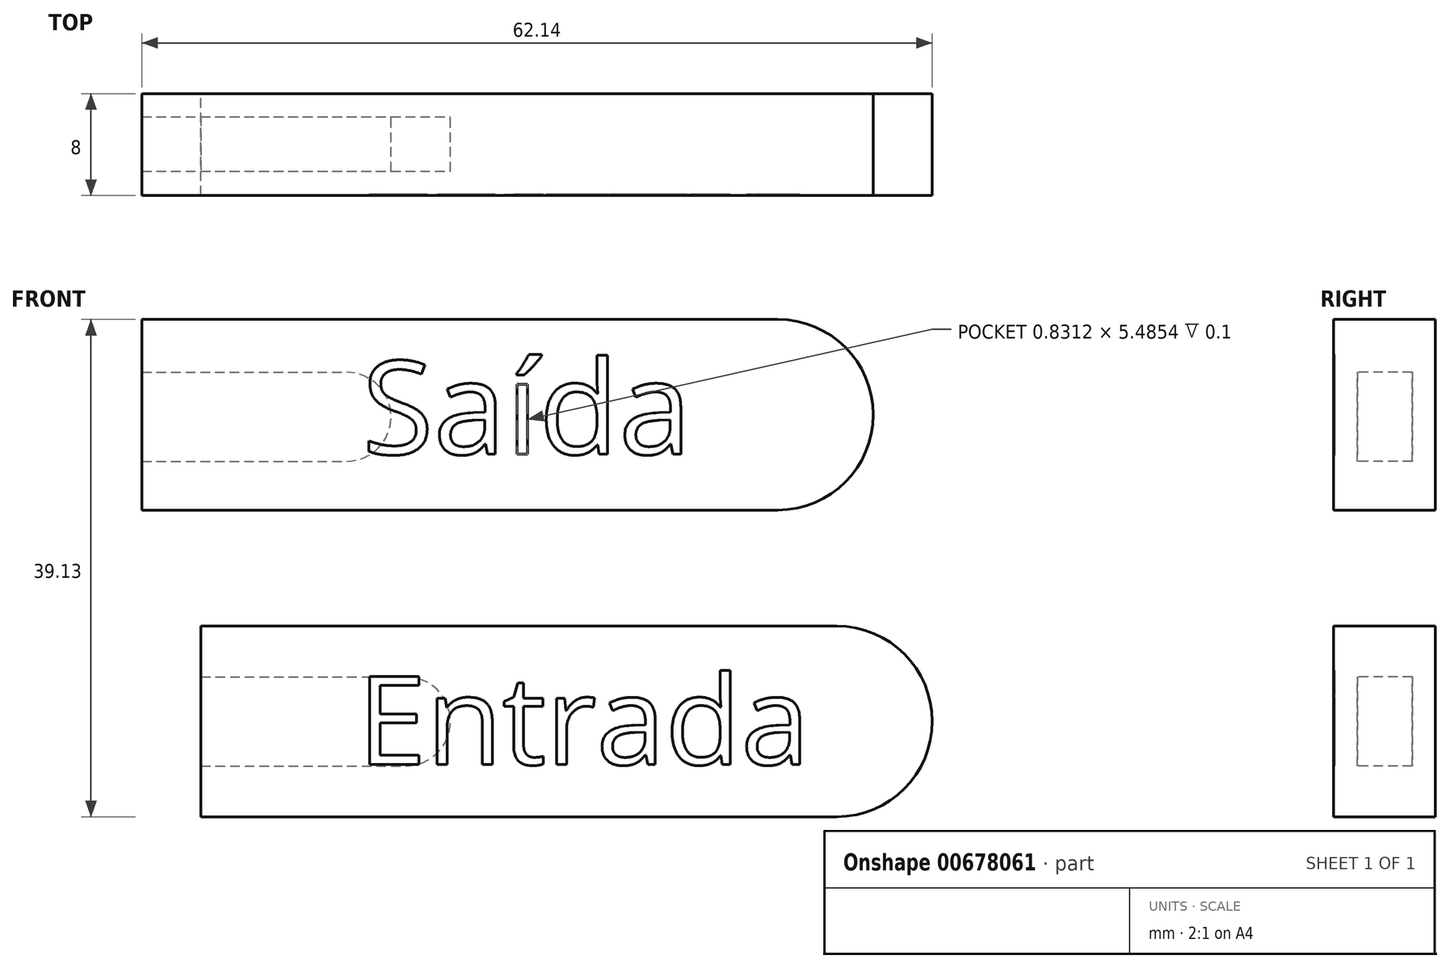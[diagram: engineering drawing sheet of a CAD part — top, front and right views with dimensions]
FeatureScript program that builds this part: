
annotation { "Feature Type Name" : "Feature", "Feature Type Description" : "" }
export const myFeature = defineFeature(function(context is Context, id is Id, definition is map)
    precondition{}
    {
        {
            var Q0;
            Q0=qCreatedBy(makeId("Front.planeOp"),FACE);
            var sketch = newSketch(context, id + "F0", { "sketchPlane" : qUnion([Q0])});
            skLineSegment(sketch, "E0", {"start": v(-53.67, -9.13) * mm, "end": v(-53.67, -24.13) * mm});
            skLineSegment(sketch, "E1", {"start": v(-53.67, -9.13) * mm, "end": v(-3.67, -9.13) * mm});
            skLineSegment(sketch, "E2", {"start": v(-53.67, -24.13) * mm, "end": v(-3.67, -24.13) * mm});
            skArc(sketch, "E3", {"start": v(-3.67, -24.13) * mm, "mid": v(3.83, -16.63) * mm, "end": v(-3.67, -9.13) * mm});
            skSolve(sketch);
        }
        {
            var Q0;
            Q0=makeQuery(id+"F0.imprint","IMPRINT",FACE,{"disambiguationData":[TD([[makeQuery(id+"F0.imprint","IMPRINT",EDGE,{"derivedFrom":sQuery(id+"F0.wireOp",EDGE,"E0")}),1.0]])]});
            extrude(context, id + "F1", {"entities" : qUnion([Q0]), "depth" : 8 * mm, "offsetDistance" : 25.4 * mm});
        }
        {
            var Q0;
            Q0=qCreatedBy(makeId("Front.planeOp"),FACE);
            var sketch = newSketch(context, id + "F2", { "sketchPlane" : qUnion([Q0])});
            skLineSegment(sketch, "E4", {"start": v(-53.76, -13.13) * mm, "end": v(-53.76, -20.13) * mm});
            skLineSegment(sketch, "E5", {"start": v(-53.76, -20.13) * mm, "end": v(-37.56, -20.13) * mm});
            skLineSegment(sketch, "E6", {"start": v(-53.76, -13.13) * mm, "end": v(-37.56, -13.13) * mm});
            skArc(sketch, "E7", {"start": v(-37.56, -13.13) * mm, "mid": v(-34.06, -16.63) * mm, "end": v(-37.56, -20.13) * mm});
            skSolve(sketch);
        }
        {
            var Q0;
            Q0 = qSketchRegion(id + "F2", true);
            var Q1;
            Q1 = qSketchRegion(id + "F4", true);
            extrude(context, id + "F3", {"entities" : qUnion([Q0, Q1]), "operationType" : NewBodyOperationType.REMOVE, "depth" : 6.1 * mm, "offsetDistance" : 25.4 * mm, "hasSecondDirection" : true, "secondDirectionOppositeDirection" : false, "secondDirectionDepth" : 1.8 * mm});
        }
        {
            var Q0;
            Q0=makeQuery(id+"F1.opExtrude","CAP_FACE",FACE,{"disambiguationData":[OSD([sQuery(id+"F0.wireOp",EDGE,"E0"),sQuery(id+"F0.wireOp",EDGE,"E1"),sQuery(id+"F0.wireOp",EDGE,"E2"),sQuery(id+"F0.wireOp",EDGE,"E3")])],"isStart":false});
            var sketch = newSketch(context, id + "F4", { "sketchPlane" : qUnion([Q0])});
            skText(sketch, "E8", { "text": "Entrada\n", "fontName": "OpenSans-Regular.ttf"});
            const initialGuessF4  = {"E8": [-0.04135, -0.02002, 1, 0, 0.007]};
            skSetInitialGuess(sketch, initialGuessF4);
            skSolve(sketch);
        }
        {
            var Q0;
            Q0 = qSketchRegion(id + "F4", true);
            extrude(context, id + "F5", {"entities" : qUnion([Q0]), "operationType" : NewBodyOperationType.REMOVE, "oppositeDirection" : true, "depth" : 0.1 * mm, "offsetDistance" : 25.4 * mm});
        }
        {
            var Q0;
            Q0=qCreatedBy(makeId("Front.planeOp"),FACE);
            var sketch = newSketch(context, id + "F6", { "sketchPlane" : qUnion([Q0])});
            skLineSegment(sketch, "E9", {"start": v(-58.3, 15) * mm, "end": v(-58.3, 0) * mm});
            skLineSegment(sketch, "E10", {"start": v(-58.3, 15) * mm, "end": v(-8.3, 15) * mm});
            skLineSegment(sketch, "E11", {"start": v(-58.3, 0) * mm, "end": v(-8.3, 0) * mm});
            skArc(sketch, "E12", {"start": v(-8.3, 0) * mm, "mid": v(-0.8, 7.5) * mm, "end": v(-8.3, 15) * mm});
            skSolve(sketch);
        }
        {
            var Q0;
            Q0 = qSketchRegion(id + "F6", true);
            extrude(context, id + "F7", {"entities" : qUnion([Q0]), "depth" : 8 * mm, "offsetDistance" : 25.4 * mm});
        }
        {
            var Q0;
            Q0=qCreatedBy(makeId("Front.planeOp"),FACE);
            var sketch = newSketch(context, id + "F8", { "sketchPlane" : qUnion([Q0])});
            skLineSegment(sketch, "E13", {"start": v(-58.42, 10.84) * mm, "end": v(-58.42, 3.84) * mm});
            skLineSegment(sketch, "E14", {"start": v(-58.42, 3.84) * mm, "end": v(-42.22, 3.84) * mm});
            skLineSegment(sketch, "E15", {"start": v(-58.42, 10.84) * mm, "end": v(-42.22, 10.84) * mm});
            skArc(sketch, "E16", {"start": v(-42.22, 3.84) * mm, "mid": v(-38.72, 7.34) * mm, "end": v(-42.22, 10.84) * mm});
            skSolve(sketch);
        }
        {
            var Q0;
            Q0=makeQuery(id+"F8.imprint","IMPRINT",FACE,{"disambiguationData":[TD([[makeQuery(id+"F8.imprint","IMPRINT",EDGE,{"derivedFrom":sQuery(id+"F8.wireOp",EDGE,"E13")}),1.0]])]});
            extrude(context, id + "F9", {"entities" : qUnion([Q0]), "operationType" : NewBodyOperationType.REMOVE, "depth" : 6.1 * mm, "offsetDistance" : 25.4 * mm, "hasSecondDirection" : true, "secondDirectionOppositeDirection" : false, "secondDirectionDepth" : 1.8 * mm});
        }
        {
            var Q0;
            Q0=makeQuery(id+"F7.opExtrude","CAP_FACE",FACE,{"disambiguationData":[OSD([sQuery(id+"F6.wireOp",EDGE,"E9"),sQuery(id+"F6.wireOp",EDGE,"E10"),sQuery(id+"F6.wireOp",EDGE,"E11"),sQuery(id+"F6.wireOp",EDGE,"E12")])],"isStart":false});
            var sketch = newSketch(context, id + "F10", { "sketchPlane" : qUnion([Q0])});
            skText(sketch, "E17", { "text": "Saída", "fontName": "OpenSans-Regular.ttf"});
            const initialGuessF10  = {"E17": [-0.04101, 0.0044, 1, 0, 0.00738]};
            skSetInitialGuess(sketch, initialGuessF10);
            skSolve(sketch);
        }
        {
            var Q0;
            Q0 = qSketchRegion(id + "F10", true);
            extrude(context, id + "F11", {"entities" : qUnion([Q0]), "operationType" : NewBodyOperationType.REMOVE, "oppositeDirection" : true, "depth" : 0.1 * mm, "offsetDistance" : 25.4 * mm});
        }
    });
